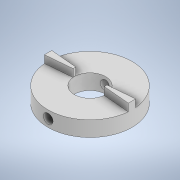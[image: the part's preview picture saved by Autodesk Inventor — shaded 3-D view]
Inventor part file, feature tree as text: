
AUTODESK INVENTOR PART (.ipt)
format: ipt  version: 2021 (Build 250183000, 183)  size: 143,872 bytes
history: native  units: mm
features: extrude x3, sketch x2, pattern_circular x1
ambient origin geometry x8: Origin, YZ Plane, XZ Plane, XY Plane, X Axis, Y Axis, Z Axis, Center Point
bodies: Solid1 (feature_tree)
feature tree (6):
  extrude  "Extrusion1"  Depth=22.0mm
  extrude  "Extrusion2"  Depth=2.0mm
  extrude  "Extrusion3"  Depth=2.0mm TaperAngle=0.0deg
  pattern_circular  "Circular Pattern1"  [2 undecoded]
  sketch  "Sketch1"  dims[d0=8.2mm d1=22.0mm]
  sketch  "Sketch3"  dims[d2=4.0mm d3=0.0mm d4=1.745329mm d5=2.0mm d6=0.0mm d7=2.5mm d8=2.0mm d9=12.75mm d10=0.0mm d11=20.0mm d12=360.0deg]
note: 2 required parameter values undecoded (feature->parameter linkage not recoverable at this tier; creation-order binding heuristic only, values carry confidence <= 0.55)
